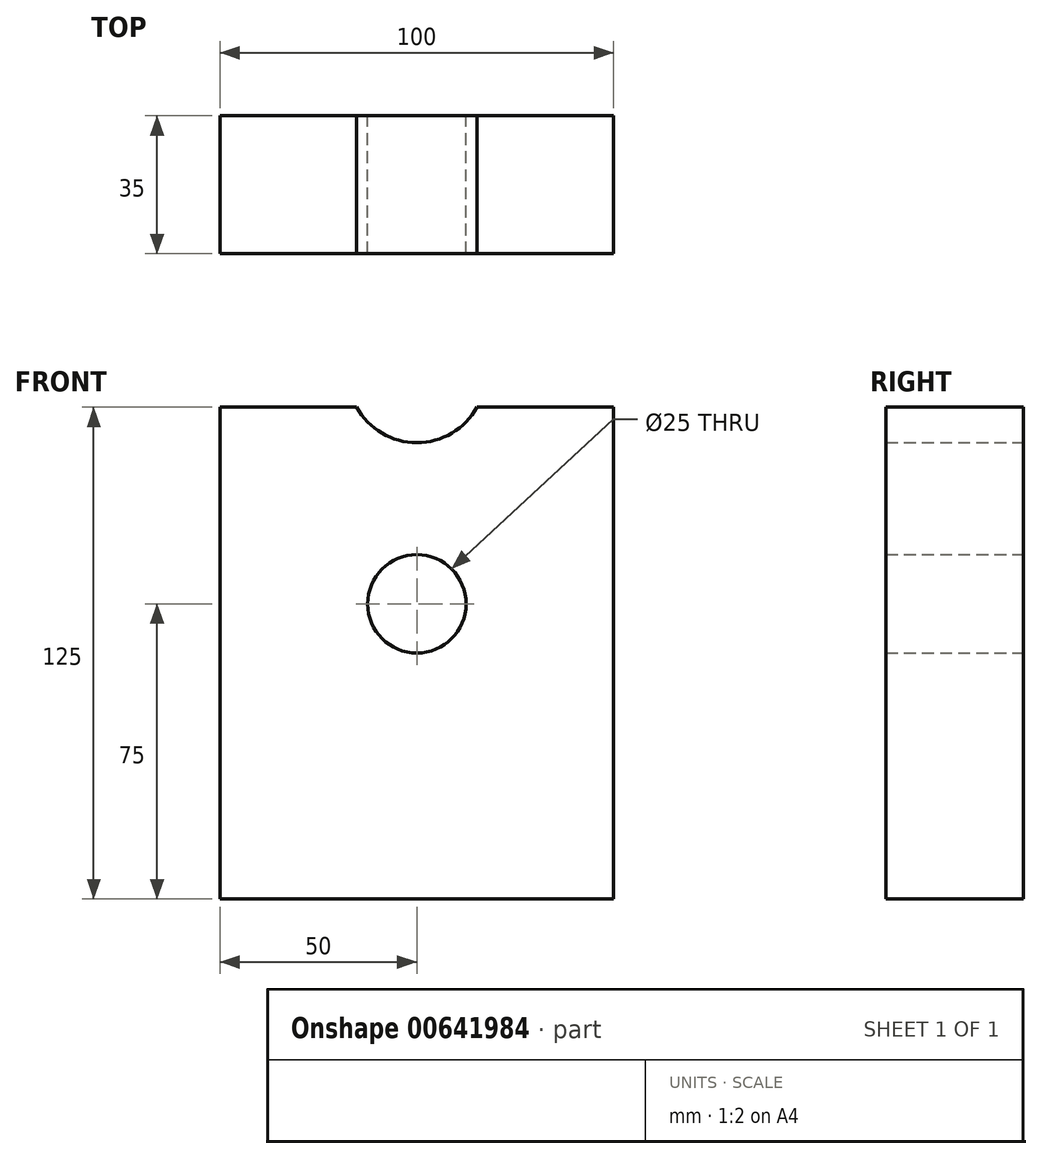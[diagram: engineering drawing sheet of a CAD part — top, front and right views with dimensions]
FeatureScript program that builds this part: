
annotation { "Feature Type Name" : "Feature", "Feature Type Description" : "" }
export const myFeature = defineFeature(function(context is Context, id is Id, definition is map)
    precondition{}
    {
        {
            var Q0;
            Q0=qCreatedBy(makeId("Front.planeOp"),FACE);
            var sketch = newSketch(context, id + "F0", { "sketchPlane" : qUnion([Q0])});
            skLineSegment(sketch, "E0.bottom", {"start": v(50, 0) * mm, "end": v(-50, 0) * mm});
            skLineSegment(sketch, "E0.top", {"start": v(50, 125) * mm, "end": v(15.32, 125) * mm});
            skLineSegment(sketch, "E0.left", {"start": v(50, 0) * mm, "end": v(50, 125) * mm});
            skLineSegment(sketch, "E0.right", {"start": v(-50, 0) * mm, "end": v(-50, 125) * mm});
            skCircle(sketch, "E1", {"center": v(0, 75) * mm, "radius": 12.5 * mm});
            skCircle(sketch, "E2", {"center": v(0, 133.45) * mm, "radius": 12.5 * mm, "construction": true});
            skCircle(sketch, "E3", {"center": v(-22.5, 110) * mm, "radius": 20 * mm, "construction": true});
            skCircle(sketch, "E4", {"center": v(22.5, 110) * mm, "radius": 20 * mm, "construction": true});
            skLineSegment(sketch, "E5", {"start": v(-22.5, 110) * mm, "end": v(22.5, 110) * mm, "construction": true});
            skLineSegment(sketch, "E6", {"start": v(0, 0) * mm, "end": v(0, 110) * mm, "construction": true});
            skLineSegment(sketch, "E7", {"start": v(0, 110) * mm, "end": v(0, 110) * mm});
            skArc(sketch, "E8", {"start": v(-15.32, 125) * mm, "mid": v(0, 115.95) * mm, "end": v(15.32, 125) * mm});
            skLineSegment(sketch, "E9.trimOffspring", {"start": v(-15.32, 125) * mm, "end": v(-50, 125) * mm});
            skSolve(sketch);
        }
        {
            var Q0;
            Q0 = qSketchRegion(id + "F0", true);
            extrude(context, id + "F1", {"entities" : qUnion([Q0]), "endBound" : BoundingType.SYMMETRIC, "depth" : 35 * mm, "offsetDistance" : 25 * mm});
        }
    });
